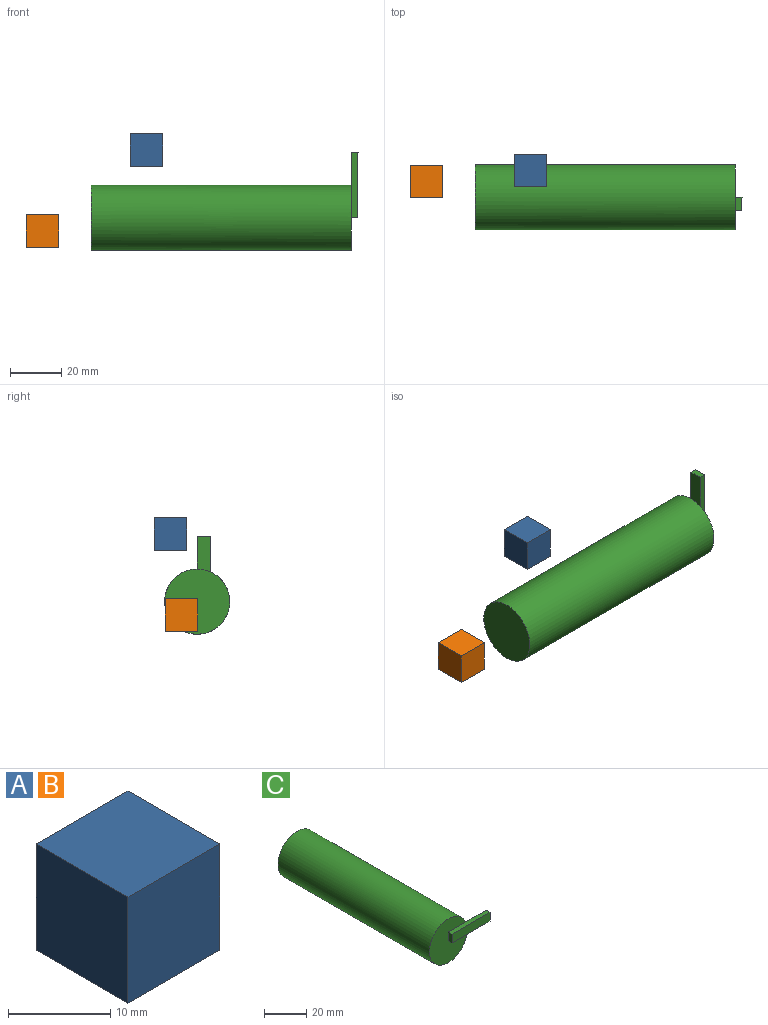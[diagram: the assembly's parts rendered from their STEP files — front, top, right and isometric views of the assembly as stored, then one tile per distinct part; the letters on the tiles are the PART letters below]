
ASSEMBLY  parts=3 mates=1
PART A: 6 faces, bbox 12.7x12.7x12.7 mm
  f0: plane 12.7x12.7mm, normal (0,0,-1), area 161.3mm2, adj f1,f3,f4,f5
  f1: plane 12.7x12.7mm, normal (1,0,0), area 161.3mm2, adj f0,f2,f4,f5
  f2: plane 12.7x12.7mm, normal (0,0,1), area 161.3mm2, adj f1,f3,f4,f5
  f3: plane 12.7x12.7mm, normal (-1,0,0), area 161.3mm2, adj f0,f2,f4,f5
  f4: plane 12.7x12.7mm, normal (0,-1,0), area 161.3mm2, adj f0,f1,f2,f3
  f5: plane 12.7x12.7mm, normal (0,1,0), area 161.3mm2, adj f0,f1,f2,f3
PART B: same geometry as A
PART C: 9 faces, bbox 38.1x104.1x25.4 mm
  f0: plane 25.4x25.4mm, normal (0,-1,0), area 444mm2, adj f1,f4,f5,f6
  f1: cylinder r=12.7mm len=101.6mm, axis (0,1,0), area 8107.3mm2, adj f0,f2,f3
  f2: plane 25.4x25.4mm, normal (0,1,0), area 506.7mm2, adj f1
  f3: plane 13.76x5.08mm, normal (0,1,0), area 66.3mm2, adj f1,f4,f6,f7
  f4: plane 25.4x2.54mm, normal (0,0,1), area 64.5mm2, adj f0,f3,f5,f7,f8
  f5: plane 5.08x2.54mm, normal (-1,0,0), area 12.9mm2, adj f0,f4,f6,f8
  f6: plane 25.4x2.54mm, normal (0,0,-1), area 64.5mm2, adj f0,f3,f5,f7,f8
  f7: plane 5.08x2.54mm, normal (1,0,0), area 12.9mm2, adj f3,f4,f6,f8
  f8: plane 25.4x5.08mm, normal (0,-1,0), area 129mm2, adj f4,f5,f6,f7
PLACE A rot(axis=(0,0,1),90deg) t=(-3.23,45.5,-44.38)mm
PLACE B rot(axis=(0.58,-0.58,-0.58),120deg) t=(-9.01,41.3,-41.03)mm
PLACE C rot(axis=(0.58,-0.58,0.58),120deg) t=(-18.54,35.11,-42.18)mm
MATE planar B.f2 <-> C.f1  axis (-1,0,0) through (-43.94,41.3,-47.38)mm
